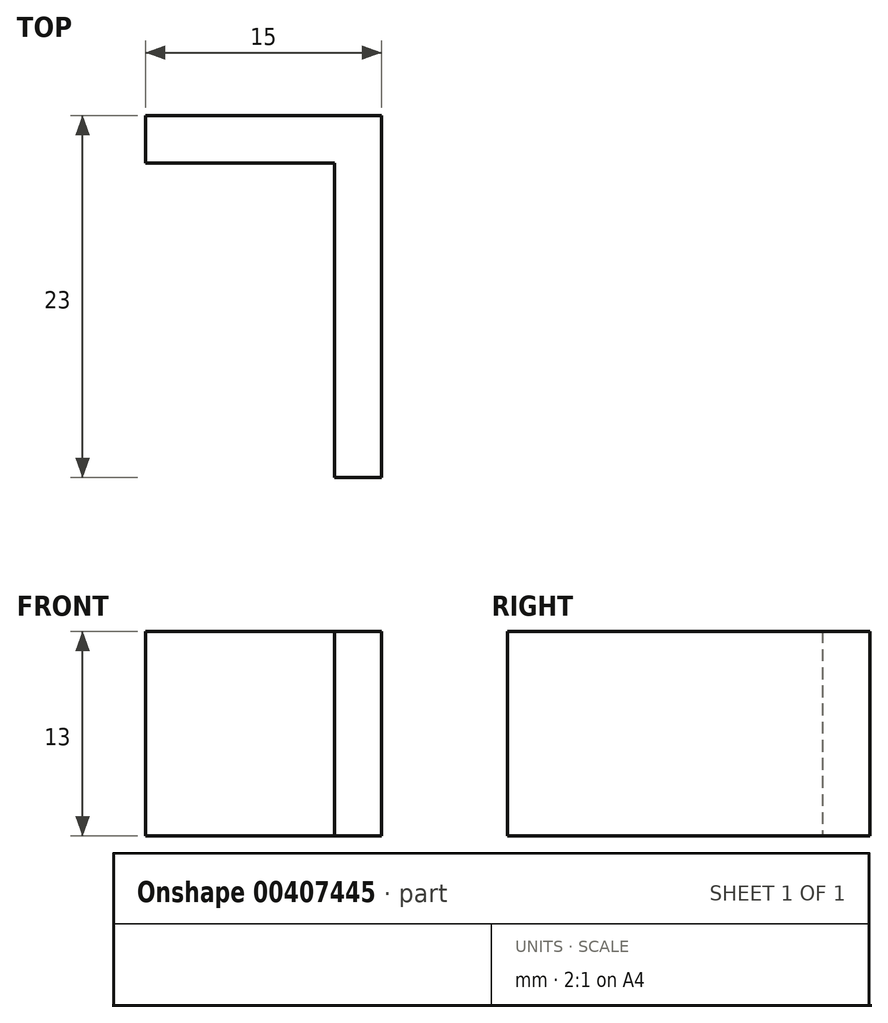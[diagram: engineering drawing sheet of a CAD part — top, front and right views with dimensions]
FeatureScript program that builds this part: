
annotation { "Feature Type Name" : "Feature", "Feature Type Description" : "" }
export const myFeature = defineFeature(function(context is Context, id is Id, definition is map)
    precondition{}
    {
        {
            var Q0;
            Q0=qCreatedBy(makeId("Top.planeOp"),FACE);
            var sketch = newSketch(context, id + "F0", { "sketchPlane" : qUnion([Q0])});
            skLineSegment(sketch, "E0.bottom", {"start": v(1.5, -10) * mm, "end": v(-1.5, -10) * mm});
            skLineSegment(sketch, "E0.top", {"start": v(1.5, 10) * mm, "end": v(-1.5, 10) * mm});
            skLineSegment(sketch, "E0.left", {"start": v(1.5, -10) * mm, "end": v(1.5, 10) * mm});
            skLineSegment(sketch, "E0.right", {"start": v(-1.5, -10) * mm, "end": v(-1.5, 10) * mm});
            skPoint(sketch, "E0.middle", {"position": v(0, 0) * mm});
            skLineSegment(sketch, "E1.bottom", {"start": v(1.5, 10) * mm, "end": v(-13.5, 10) * mm});
            skLineSegment(sketch, "E1.top", {"start": v(1.5, 13) * mm, "end": v(-13.5, 13) * mm});
            skLineSegment(sketch, "E1.left", {"start": v(1.5, 10) * mm, "end": v(1.5, 13) * mm});
            skLineSegment(sketch, "E1.right", {"start": v(-13.5, 10) * mm, "end": v(-13.5, 13) * mm});
            skSolve(sketch);
        }
        {
            var Q0;
            Q0=makeQuery(id+"F0.imprint","IMPRINT",FACE,{"disambiguationData":[TD([[makeQuery(id+"F0.imprint","IMPRINT",EDGE,{"derivedFrom":sQuery(id+"F0.wireOp",EDGE,"E0.bottom")}),-1.0]])]});
            var Q1;
            Q1=makeQuery(id+"F0.imprint","IMPRINT",FACE,{"disambiguationData":[TD([[makeQuery(id+"F0.imprint","IMPRINT",EDGE,{"derivedFrom":sQuery(id+"F0.wireOp",EDGE,"E1.top")}),1.0]])]});
            extrude(context, id + "F1", {"entities" : qUnion([Q0, Q1]), "depth" : 13 * mm});
        }
    });
